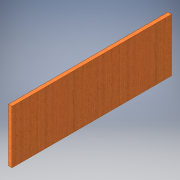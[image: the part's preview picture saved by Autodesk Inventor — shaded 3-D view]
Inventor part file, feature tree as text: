
AUTODESK INVENTOR PART (.ipt)
format: ipt  version: 2016 (Build 200138000, 138)  size: 104,448 bytes
history: native  units: in
note: dims shown in document units (in); Inventor stores cm internally (conversion verified against a paired STEP export)
features: extrude x1, sketch x1
ambient origin geometry x8: Origin, YZ Plane, XZ Plane, XY Plane, X Axis, Y Axis, Z Axis, Center Point
bodies: Solid1 (feature_tree)
feature tree (2):
  extrude  "Extrusion1"  Depth=6.5in
  sketch  "Sketch1"  dims[d0=19.5in d1=6.5in d2=0.4375in d3=0.0in]
